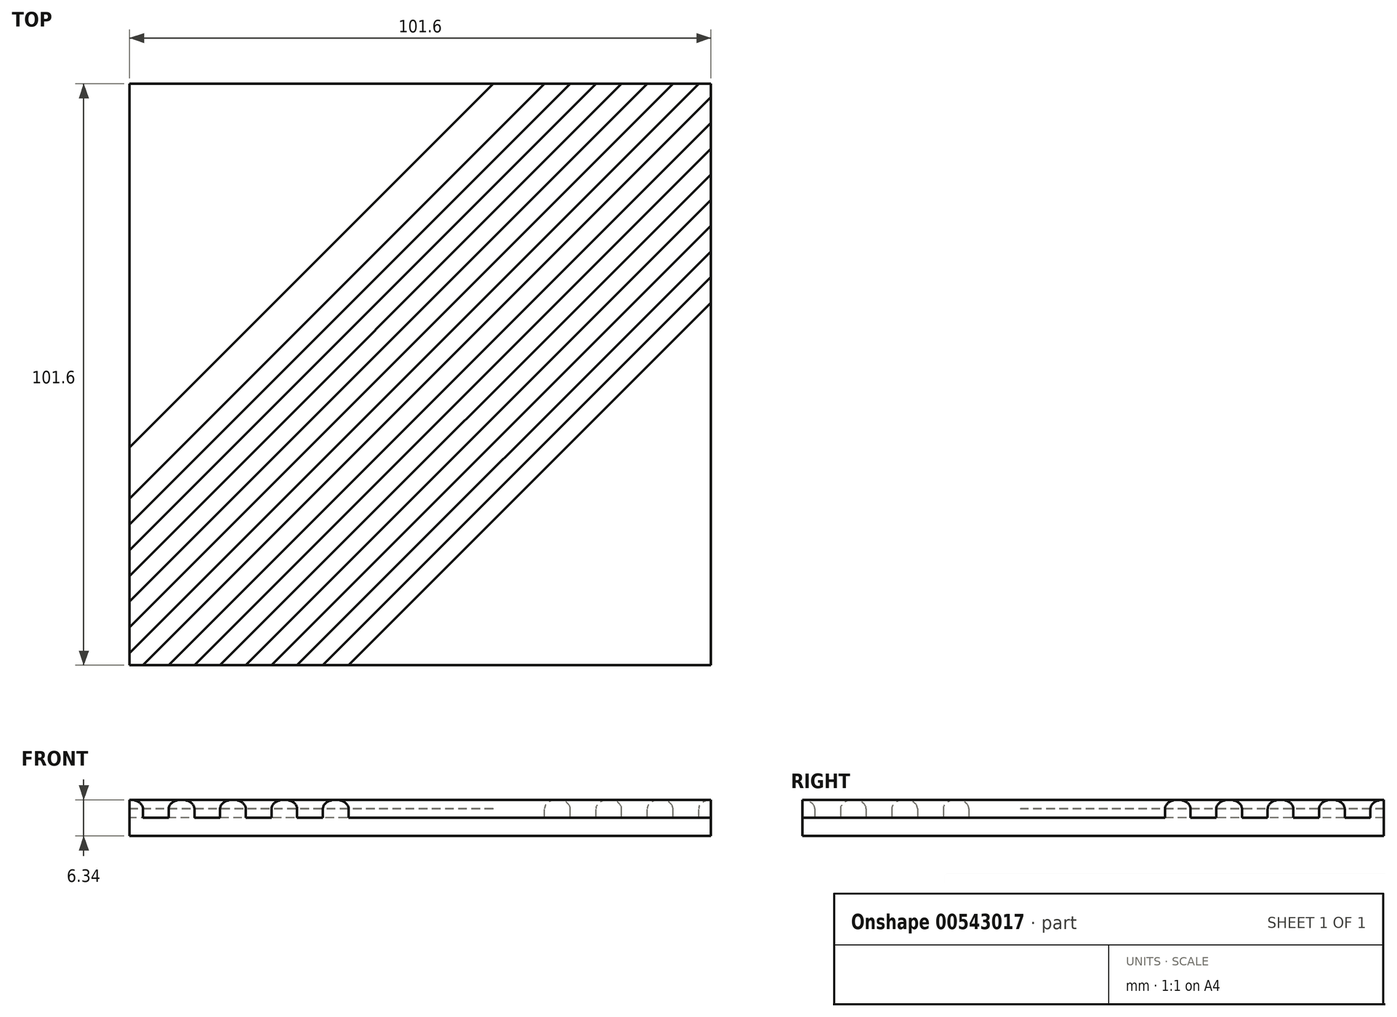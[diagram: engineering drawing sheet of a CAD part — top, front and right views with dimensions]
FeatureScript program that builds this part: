
annotation { "Feature Type Name" : "Feature", "Feature Type Description" : "" }
export const myFeature = defineFeature(function(context is Context, id is Id, definition is map)
    precondition{}
    {
        {
            var Q0;
            Q0=qCreatedBy(makeId("Top.planeOp"),FACE);
            var sketch = newSketch(context, id + "F0", { "sketchPlane" : qUnion([Q0])});
            skLineSegment(sketch, "E0.bottom", {"start": v(50.8, 50.8) * mm, "end": v(-50.8, 50.8) * mm});
            skLineSegment(sketch, "E0.top", {"start": v(50.8, -50.8) * mm, "end": v(-50.8, -50.8) * mm});
            skLineSegment(sketch, "E0.left", {"start": v(50.8, 50.8) * mm, "end": v(50.8, -50.8) * mm});
            skLineSegment(sketch, "E0.right", {"start": v(-50.8, 50.8) * mm, "end": v(-50.8, -50.8) * mm});
            skPoint(sketch, "E0.middle", {"position": v(0, 0) * mm});
            skSolve(sketch);
        }
        {
            var Q0;
            Q0=makeQuery(id+"F0.imprint","IMPRINT",FACE,{"disambiguationData":[TD([[makeQuery(id+"F0.imprint","IMPRINT",EDGE,{"derivedFrom":sQuery(id+"F0.wireOp",EDGE,"E0.bottom")}),1.0]])]});
            extrude(context, id + "F1", {"entities" : qUnion([Q0]), "depth" : 3.17 * mm, "offsetDistance" : 25.4 * mm});
        }
        {
            var Q0;
            Q0=makeQuery(id+"F1.opExtrude","CAP_FACE",FACE,{"disambiguationData":[OSD([sQuery(id+"F0.wireOp",EDGE,"E0.bottom"),sQuery(id+"F0.wireOp",EDGE,"E0.top"),sQuery(id+"F0.wireOp",EDGE,"E0.left"),sQuery(id+"F0.wireOp",EDGE,"E0.right")])],"isStart":false});
            var sketch = newSketch(context, id + "F2", { "sketchPlane" : qUnion([Q0])});
            skLineSegment(sketch, "E1", {"start": v(-50.8, -50.8) * mm, "end": v(50.8, 50.8) * mm});
            skLineSegment(sketch, "E2.0", {"start": v(-41.82, -50.8) * mm, "end": v(50.8, 41.82) * mm});
            skLineSegment(sketch, "E3.0", {"start": v(-32.84, -50.8) * mm, "end": v(50.8, 32.84) * mm});
            skLineSegment(sketch, "E4.0", {"start": v(-23.86, -50.8) * mm, "end": v(50.8, 23.86) * mm});
            skLineSegment(sketch, "E5.0", {"start": v(-14.88, -50.8) * mm, "end": v(50.8, 14.88) * mm});
            skLineSegment(sketch, "E6.0", {"start": v(-50.8, -41.82) * mm, "end": v(41.82, 50.8) * mm});
            skLineSegment(sketch, "E7.0", {"start": v(-50.8, -32.84) * mm, "end": v(32.84, 50.8) * mm});
            skLineSegment(sketch, "E8.0", {"start": v(-50.8, -23.86) * mm, "end": v(23.86, 50.8) * mm});
            skLineSegment(sketch, "E9.0", {"start": v(-50.8, -14.88) * mm, "end": v(14.88, 50.8) * mm});
            skLineSegment(sketch, "E10.0", {"start": v(-50.8, 50.8) * mm, "end": v(-50.8, -50.8) * mm});
            skLineSegment(sketch, "E11.0", {"start": v(50.8, -50.8) * mm, "end": v(-50.8, -50.8) * mm});
            skLineSegment(sketch, "E12.0", {"start": v(50.8, 50.8) * mm, "end": v(50.8, -50.8) * mm});
            skLineSegment(sketch, "E13.0", {"start": v(50.8, 50.8) * mm, "end": v(-50.8, 50.8) * mm});
            skSolve(sketch);
        }
        {
            var Q0;
            Q0=sQuery(id+"F2.wireOp",EDGE,"E1");
            cPlane(context, id + "F3", {"entities" : qUnion([Q0]), "cplaneType" : CPlaneType.MID_PLANE, "offset" : 25.4 * mm, "width" : 152.4 * mm, "height" : 152.4 * mm});
        }
        {
            var Q0;
            Q0=qCreatedBy(id+"F3.planeOp",FACE);
            var sketch = newSketch(context, id + "F4", { "sketchPlane" : qUnion([Q0])});
            skArc(sketch, "E14", {"start": v(26.92, 4.74) * mm, "mid": v(25.33, 6.34) * mm, "end": v(23.74, 4.75) * mm});
            skLineSegment(sketch, "E15.direction1", {"start": v(25.33, 4.75) * mm, "end": v(18.98, 4.75) * mm, "construction": true});
            skLineSegment(sketch, "E16", {"start": v(26.92, 4.76) * mm, "end": v(26.92, 3.18) * mm});
            skLineSegment(sketch, "E17", {"start": v(23.74, 4.75) * mm, "end": v(23.74, 3.18) * mm});
            skLineSegment(sketch, "E18", {"start": v(26.92, 3.18) * mm, "end": v(23.74, 3.18) * mm});
            skLineSegment(sketch, "E19.1.0.0", {"start": v(17.4, 4.75) * mm, "end": v(17.4, 3.18) * mm});
            skLineSegment(sketch, "E19.1.0.1", {"start": v(20.57, 3.18) * mm, "end": v(17.4, 3.18) * mm});
            skLineSegment(sketch, "E19.1.0.2", {"start": v(20.57, 4.76) * mm, "end": v(20.57, 3.18) * mm});
            skArc(sketch, "E19.1.0.3", {"start": v(20.57, 4.74) * mm, "mid": v(18.98, 6.34) * mm, "end": v(17.4, 4.75) * mm});
            skLineSegment(sketch, "E19.2.0.0", {"start": v(11.04, 4.75) * mm, "end": v(11.04, 3.18) * mm});
            skLineSegment(sketch, "E19.2.0.1", {"start": v(14.22, 3.18) * mm, "end": v(11.04, 3.18) * mm});
            skLineSegment(sketch, "E19.2.0.2", {"start": v(14.22, 4.76) * mm, "end": v(14.22, 3.18) * mm});
            skArc(sketch, "E19.2.0.3", {"start": v(14.22, 4.74) * mm, "mid": v(12.63, 6.34) * mm, "end": v(11.04, 4.75) * mm});
            skLineSegment(sketch, "E19.3.0.0", {"start": v(4.7, 4.75) * mm, "end": v(4.7, 3.18) * mm});
            skLineSegment(sketch, "E19.3.0.1", {"start": v(7.87, 3.18) * mm, "end": v(4.7, 3.18) * mm});
            skLineSegment(sketch, "E19.3.0.2", {"start": v(7.87, 4.76) * mm, "end": v(7.87, 3.18) * mm});
            skArc(sketch, "E19.3.0.3", {"start": v(7.87, 4.74) * mm, "mid": v(6.28, 6.34) * mm, "end": v(4.7, 4.75) * mm});
            skLineSegment(sketch, "E19.4.0.0", {"start": v(-1.66, 4.75) * mm, "end": v(-1.66, 3.18) * mm});
            skLineSegment(sketch, "E19.4.0.1", {"start": v(1.52, 3.18) * mm, "end": v(-1.66, 3.18) * mm});
            skLineSegment(sketch, "E19.4.0.2", {"start": v(1.52, 4.76) * mm, "end": v(1.52, 3.18) * mm});
            skArc(sketch, "E19.4.0.3", {"start": v(1.52, 4.74) * mm, "mid": v(-0.07, 6.34) * mm, "end": v(-1.66, 4.75) * mm});
            skLineSegment(sketch, "E19.5.0.0", {"start": v(-8, 4.75) * mm, "end": v(-8, 3.18) * mm});
            skLineSegment(sketch, "E19.5.0.1", {"start": v(-4.83, 3.18) * mm, "end": v(-8, 3.18) * mm});
            skLineSegment(sketch, "E19.5.0.2", {"start": v(-4.83, 4.76) * mm, "end": v(-4.83, 3.18) * mm});
            skArc(sketch, "E19.5.0.3", {"start": v(-4.83, 4.74) * mm, "mid": v(-6.42, 6.34) * mm, "end": v(-8, 4.75) * mm});
            skLineSegment(sketch, "E19.6.0.0", {"start": v(-14.36, 4.75) * mm, "end": v(-14.36, 3.18) * mm});
            skLineSegment(sketch, "E19.6.0.1", {"start": v(-11.18, 3.18) * mm, "end": v(-14.36, 3.18) * mm});
            skLineSegment(sketch, "E19.6.0.2", {"start": v(-11.18, 4.76) * mm, "end": v(-11.18, 3.18) * mm});
            skArc(sketch, "E19.6.0.3", {"start": v(-11.18, 4.74) * mm, "mid": v(-12.77, 6.34) * mm, "end": v(-14.36, 4.75) * mm});
            skLineSegment(sketch, "E19.7.0.0", {"start": v(-20.7, 4.75) * mm, "end": v(-20.7, 3.18) * mm});
            skLineSegment(sketch, "E19.7.0.1", {"start": v(-17.53, 3.18) * mm, "end": v(-20.7, 3.18) * mm});
            skLineSegment(sketch, "E19.7.0.2", {"start": v(-17.53, 4.76) * mm, "end": v(-17.53, 3.18) * mm});
            skArc(sketch, "E19.7.0.3", {"start": v(-17.53, 4.74) * mm, "mid": v(-19.12, 6.34) * mm, "end": v(-20.7, 4.75) * mm});
            skLineSegment(sketch, "E19.8.0.0", {"start": v(-27.06, 4.75) * mm, "end": v(-27.06, 3.18) * mm});
            skLineSegment(sketch, "E19.8.0.1", {"start": v(-23.88, 3.18) * mm, "end": v(-27.06, 3.18) * mm});
            skLineSegment(sketch, "E19.8.0.2", {"start": v(-23.88, 4.76) * mm, "end": v(-23.88, 3.18) * mm});
            skArc(sketch, "E19.8.0.3", {"start": v(-23.88, 4.74) * mm, "mid": v(-25.47, 6.34) * mm, "end": v(-27.06, 4.75) * mm});
            skLineSegment(sketch, "E19.direction1", {"start": v(23.74, 3.18) * mm, "end": v(17.4, 3.18) * mm, "construction": true});
            skSolve(sketch);
        }
        {
            var Q0;
            Q0=makeQuery(id+"F4.imprint","IMPRINT",FACE,{"disambiguationData":[TD([[makeQuery(id+"F4.imprint","IMPRINT",EDGE,{"derivedFrom":sQuery(id+"F4.wireOp",EDGE,"E14")}),1.0]])]});
            extrude(context, id + "F5", {"entities" : qUnion([Q0]), "operationType" : NewBodyOperationType.ADD, "endBound" : BoundingType.SYMMETRIC, "depth" : 101.6 * mm, "offsetDistance" : 25.4 * mm});
        }
        {
            var Q0;
            {var subQ3=sQuery(id+"F4.wireOp",EDGE,"E19.1.0.0");Q0=makeQuery(id+"F4.imprint","IMPRINT",FACE,{"disambiguationData":[TD([[makeQuery(id+"F4.imprint","IMPRINT",EDGE,{"derivedFrom":subQ3}),1.0]])]});}
            extrude(context, id + "F6", {"entities" : qUnion([Q0]), "operationType" : NewBodyOperationType.ADD, "endBound" : BoundingType.SYMMETRIC, "depth" : 114.3 * mm, "offsetDistance" : 25.4 * mm});
        }
        {
            var Q0;
            {var subQ3=sQuery(id+"F4.wireOp",EDGE,"E19.2.0.0");Q0=makeQuery(id+"F4.imprint","IMPRINT",FACE,{"disambiguationData":[TD([[makeQuery(id+"F4.imprint","IMPRINT",EDGE,{"derivedFrom":subQ3}),1.0]])]});}
            extrude(context, id + "F7", {"entities" : qUnion([Q0]), "operationType" : NewBodyOperationType.ADD, "endBound" : BoundingType.SYMMETRIC, "depth" : 127 * mm, "offsetDistance" : 25.4 * mm});
        }
        {
            var Q0;
            {var subQ3=sQuery(id+"F4.wireOp",EDGE,"E19.3.0.0");Q0=makeQuery(id+"F4.imprint","IMPRINT",FACE,{"disambiguationData":[TD([[makeQuery(id+"F4.imprint","IMPRINT",EDGE,{"derivedFrom":subQ3}),1.0]])]});}
            extrude(context, id + "F8", {"entities" : qUnion([Q0]), "operationType" : NewBodyOperationType.ADD, "endBound" : BoundingType.SYMMETRIC, "depth" : 139.7 * mm, "offsetDistance" : 25.4 * mm});
        }
        {
            var Q0;
            {var subQ3=sQuery(id+"F4.wireOp",EDGE,"E19.4.0.0");Q0=makeQuery(id+"F4.imprint","IMPRINT",FACE,{"disambiguationData":[TD([[makeQuery(id+"F4.imprint","IMPRINT",EDGE,{"derivedFrom":subQ3}),1.0]])]});}
            extrude(context, id + "F9", {"entities" : qUnion([Q0]), "operationType" : NewBodyOperationType.ADD, "endBound" : BoundingType.SYMMETRIC, "depth" : 152.4 * mm, "offsetDistance" : 25.4 * mm});
        }
        {
            var Q0;
            {var subQ3=sQuery(id+"F4.wireOp",EDGE,"E19.5.0.0");Q0=makeQuery(id+"F4.imprint","IMPRINT",FACE,{"disambiguationData":[TD([[makeQuery(id+"F4.imprint","IMPRINT",EDGE,{"derivedFrom":subQ3}),1.0]])]});}
            extrude(context, id + "F10", {"entities" : qUnion([Q0]), "operationType" : NewBodyOperationType.ADD, "endBound" : BoundingType.SYMMETRIC, "depth" : 139.7 * mm, "offsetDistance" : 25.4 * mm});
        }
        {
            var Q0;
            {var subQ3=sQuery(id+"F4.wireOp",EDGE,"E19.6.0.0");Q0=makeQuery(id+"F4.imprint","IMPRINT",FACE,{"disambiguationData":[TD([[makeQuery(id+"F4.imprint","IMPRINT",EDGE,{"derivedFrom":subQ3}),1.0]])]});}
            extrude(context, id + "F11", {"entities" : qUnion([Q0]), "operationType" : NewBodyOperationType.ADD, "endBound" : BoundingType.SYMMETRIC, "depth" : 127 * mm, "offsetDistance" : 25.4 * mm});
        }
        {
            var Q0;
            {var subQ3=sQuery(id+"F4.wireOp",EDGE,"E19.7.0.0");Q0=makeQuery(id+"F4.imprint","IMPRINT",FACE,{"disambiguationData":[TD([[makeQuery(id+"F4.imprint","IMPRINT",EDGE,{"derivedFrom":subQ3}),1.0]])]});}
            extrude(context, id + "F12", {"entities" : qUnion([Q0]), "operationType" : NewBodyOperationType.ADD, "endBound" : BoundingType.SYMMETRIC, "depth" : 114.3 * mm, "offsetDistance" : 25.4 * mm});
        }
        {
            var Q0;
            {var subQ3=sQuery(id+"F4.wireOp",EDGE,"E19.8.0.0");Q0=makeQuery(id+"F4.imprint","IMPRINT",FACE,{"disambiguationData":[TD([[makeQuery(id+"F4.imprint","IMPRINT",EDGE,{"derivedFrom":subQ3}),1.0]])]});}
            extrude(context, id + "F13", {"entities" : qUnion([Q0]), "operationType" : NewBodyOperationType.ADD, "endBound" : BoundingType.SYMMETRIC, "depth" : 101.6 * mm, "offsetDistance" : 25.4 * mm});
        }
        {
            var Q0;
            Q0=qCreatedBy(makeId("Top.planeOp"),FACE);
            var sketch = newSketch(context, id + "F14", { "sketchPlane" : qUnion([Q0])});
            skLineSegment(sketch, "E20.0", {"start": v(-50.8, 50.8) * mm, "end": v(-50.8, -50.8) * mm});
            skLineSegment(sketch, "E21", {"start": v(64.37, -66) * mm, "end": v(-62.44, -66) * mm});
            skLineSegment(sketch, "E22", {"start": v(-62.44, -66) * mm, "end": v(-62.44, 65.9) * mm});
            skLineSegment(sketch, "E23.0", {"start": v(50.8, 50.8) * mm, "end": v(-50.8, 50.8) * mm});
            skLineSegment(sketch, "E24.0", {"start": v(50.8, 50.8) * mm, "end": v(50.8, -50.8) * mm});
            skLineSegment(sketch, "E25", {"start": v(-50.8, 50.8) * mm, "end": v(50.8, 50.8) * mm});
            skLineSegment(sketch, "E26", {"start": v(-62.44, 65.9) * mm, "end": v(64.37, 65.9) * mm});
            skLineSegment(sketch, "E27", {"start": v(64.37, 65.9) * mm, "end": v(64.37, -66) * mm});
            skPoint(sketch, "E28.orphan", {"position": v(-62.44, 50.8) * mm});
            skLineSegment(sketch, "E29", {"start": v(50.8, -50.8) * mm, "end": v(-50.8, -50.8) * mm});
            skSolve(sketch);
        }
        {
            var Q0;
            Q0=makeQuery(id+"F14.imprint","IMPRINT",FACE,{"disambiguationData":[TD([[makeQuery(id+"F14.imprint","IMPRINT",EDGE,{"derivedFrom":sQuery(id+"F14.wireOp",EDGE,"E21")}),-1.0]])]});
            extrude(context, id + "F15", {"entities" : qUnion([Q0]), "operationType" : NewBodyOperationType.REMOVE, "depth" : 12.7 * mm, "offsetDistance" : 25.4 * mm});
        }
    });
